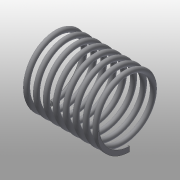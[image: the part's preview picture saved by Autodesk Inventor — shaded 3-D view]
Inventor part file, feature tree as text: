
AUTODESK INVENTOR PART (.ipt)
format: ipt  version: 2016 (Build 200138000, 138)  size: 376,320 bytes
history: native  units: mm
features: sketch x2, helix x1, extrude x1, projected_geometry x1
ambient origin geometry x8: Origin, YZ Plane, XZ Plane, XY Plane, X Axis, Y Axis, Z Axis, Center Point
bodies: Solid1 (feature_tree)
feature tree (5):
  helix  "Coil1"  [1 undecoded]
  extrude  "Extrusion1"  TaperAngle=0.0deg  [1 undecoded]
  sketch  "Sketch1"  dims[d1=7.875mm d2=0.0mm]
  sketch  "Sketch2"  dims[d3=20.0mm d4=2.5mm d5=10.0mm d6=80.0mm d7=0.0mm d8=90.0deg d9=90.0deg d10=0.0mm d11=0.0mm d12=20.0mm d13=10.0mm d14=51.25mm d15=0.0mm]
  projected_geometry  "Project Cut Edges1"
note: 2 required parameter values undecoded (feature->parameter linkage not recoverable at this tier; creation-order binding heuristic only, values carry confidence <= 0.55)
